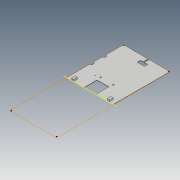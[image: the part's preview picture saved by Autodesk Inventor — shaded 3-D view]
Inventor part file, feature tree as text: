
AUTODESK INVENTOR PART (.ipt)
format: ipt  version: 2019 (Build 230136000, 136)  size: 268,288 bytes
history: native  units: mm
features: sketch x9, extrude x5, hole x3, fillet x2, plane x1
ambient origin geometry x8: Origin, YZ Plane, XZ Plane, XY Plane, X Axis, Y Axis, Z Axis, Center Point
bodies: Solid1 (feature_tree)
feature tree (20):
  sketch  "Sketch1"  dims[d3=1.0mm d6=1.0mm d7=0.0mm]
  extrude  "Extrusion1"  Depth=1.0mm TaperAngle=0.0deg
  plane  "Work Plane1"
  extrude  "Extrusion2"  Depth=6.0mm
  hole  "Hole1"  [1 undecoded]
  hole  "Hole2"  [1 undecoded]
  hole  "Hole3"  [1 undecoded]
  extrude  "Extrusion3"  Depth=2.5mm
  fillet  "Fillet1"  Radius=3.0mm
  extrude  "Extrusion5"  Depth=69.0mm
  fillet  "Fillet2"  Radius=32.0mm
  extrude  "Extrusion4"  Depth=34.5mm
  sketch  "Sketch2"  dims[d10=6.0mm d11=20.0mm]
  sketch  "Sketch4"  dims[d12=10.0mm d13=6.0mm]
  sketch  "Sketch6"  dims[d14=20.0mm d15=10.0mm]
  sketch  "Sketch7"  dims[d16=5.0mm d17=0.0mm d22=2.5mm]
  sketch  "Sketch8"  dims[d23=3.0mm d24=2.5mm d25=3.0mm]
  sketch  "Sketch9"  dims[d26=2.6mm d27=6.0mm d28=5.0mm d29=2.0mm d30=14.3117mm d31=5.0mm d32=0.0mm]
  sketch  "Sketch10"  dims[d33=2.6mm d34=6.0mm d35=5.0mm d36=2.0mm d37=14.3117mm d38=15.0mm d39=20.594885mm]
  sketch  "Sketch11"  dims[d40=2.6mm d41=6.0mm d42=5.0mm d43=2.0mm d44=14.3117mm d45=15.0mm d46=20.594885mm d47=69.0mm d48=32.0mm d52=34.5mm d53=16.0mm d54=3.5mm d55=3.5mm d56=3.5mm d57=3.5mm d59=0.0mm d62=0.0mm d64=0.0mm d65=0.0mm d66=11.0mm d67=4.8mm d68=1.0mm d69=1.0mm d70=55.0mm d71=7.0mm d72=7.0mm d73=26.0mm d74=26.0mm d75=7.0mm d76=7.0mm d77=119.0mm d78=4.5mm d79=4.5mm d80=1.0mm d81=1.0mm d82=5.0mm d83=0.0mm d84=2.0mm d85=0.0mm d86=0.0mm d87=2.0mm d88=2.0mm d89=2.0mm d90=2.0mm d91=2.0mm d92=2.0mm d93=2.0mm d94=2.0mm d95=2.0mm d96=2.0mm d97=2.0mm d98=2.0mm d99=10.0mm d100=0.0mm d101=3.0mm]
note: 3 required parameter values undecoded (feature->parameter linkage not recoverable at this tier; creation-order binding heuristic only, values carry confidence <= 0.55)
